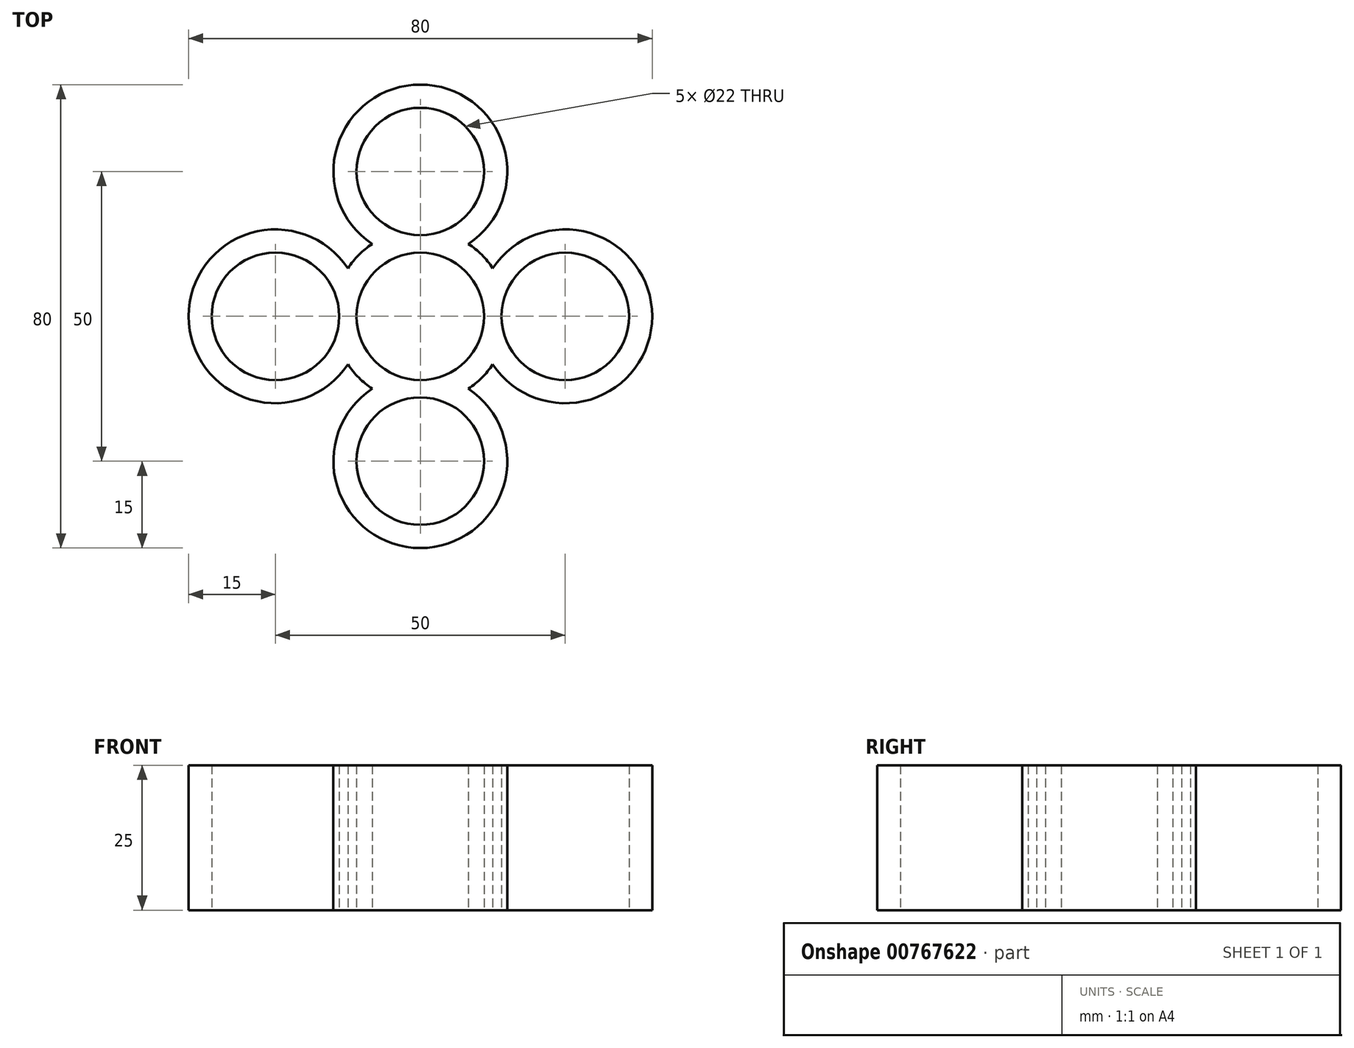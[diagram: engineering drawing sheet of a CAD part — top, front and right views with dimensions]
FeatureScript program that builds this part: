
annotation { "Feature Type Name" : "Feature", "Feature Type Description" : "" }
export const myFeature = defineFeature(function(context is Context, id is Id, definition is map)
    precondition{}
    {
        {
            var Q0;
            Q0=qCreatedBy(makeId("Top.planeOp"),FACE);
            var sketch = newSketch(context, id + "F0", { "sketchPlane" : qUnion([Q0])});
            skCircle(sketch, "E0", {"center": v(0, 0) * mm, "radius": 11 * mm});
            skArc(sketch, "E1", {"start": v(12.5, 8.3) * mm, "mid": v(10.6, 10.6) * mm, "end": v(8.3, 12.5) * mm});
            skCircle(sketch, "E2", {"center": v(-25, 0) * mm, "radius": 11 * mm});
            skArc(sketch, "E3", {"start": v(-12.5, 8.3) * mm, "mid": v(-40, 0) * mm, "end": v(-12.5, -8.3) * mm});
            skCircle(sketch, "E4", {"center": v(25, 0) * mm, "radius": 11 * mm});
            skArc(sketch, "E5", {"start": v(12.5, -8.3) * mm, "mid": v(40, 0) * mm, "end": v(12.5, 8.3) * mm});
            skCircle(sketch, "E6", {"center": v(0, 25) * mm, "radius": 11 * mm});
            skArc(sketch, "E7", {"start": v(8.3, 12.5) * mm, "mid": v(0, 40) * mm, "end": v(-8.3, 12.5) * mm});
            skCircle(sketch, "E8", {"center": v(0, -25) * mm, "radius": 11 * mm});
            skArc(sketch, "E9", {"start": v(-8.3, -12.5) * mm, "mid": v(0, -40) * mm, "end": v(8.3, -12.5) * mm});
            skArc(sketch, "E10.trimOffspring", {"start": v(8.3, -12.5) * mm, "mid": v(10.6, -10.6) * mm, "end": v(12.5, -8.3) * mm});
            skArc(sketch, "E11.trimOffspring", {"start": v(-12.5, -8.3) * mm, "mid": v(-10.6, -10.6) * mm, "end": v(-8.3, -12.5) * mm});
            skArc(sketch, "E12.trimOffspring", {"start": v(-8.3, 12.5) * mm, "mid": v(-10.6, 10.6) * mm, "end": v(-12.5, 8.3) * mm});
            skSolve(sketch);
        }
        {
            var Q0;
            Q0 = qSketchRegion(id + "F0", true);
            extrude(context, id + "F1", {"entities" : qUnion([Q0]), "depth" : 25 * mm, "offsetDistance" : 25 * mm});
        }
    });
